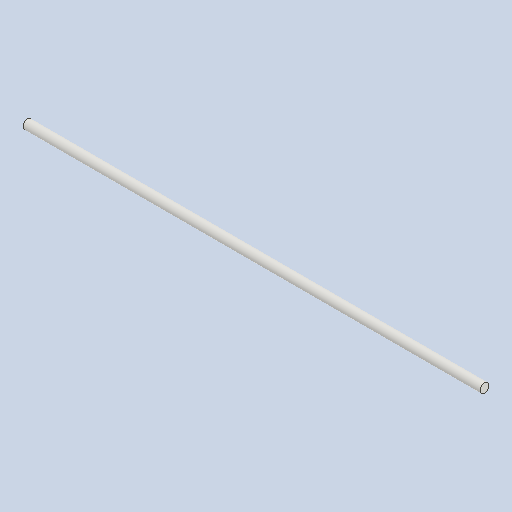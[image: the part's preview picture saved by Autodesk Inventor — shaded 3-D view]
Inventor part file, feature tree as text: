
AUTODESK INVENTOR PART (.ipt)
format: ipt  version: 2023 (Build 270158000, 158)  size: 74,752 bytes
history: native  units: mm
features: other x3, revolve x1
ambient origin geometry x6: Origin, XZ Plane, XY Plane, X Axis, Y Axis, Z Axis
bodies: Solid1 (feature_tree)
feature tree (4):
  revolve  "Revolution1"  [1 undecoded]
  other  "Start Plane"
  other  "Origin point"
  other  "Main Sketch"
note: 1 required parameter value undecoded (feature->parameter linkage not recoverable at this tier; creation-order binding heuristic only, values carry confidence <= 0.55)
